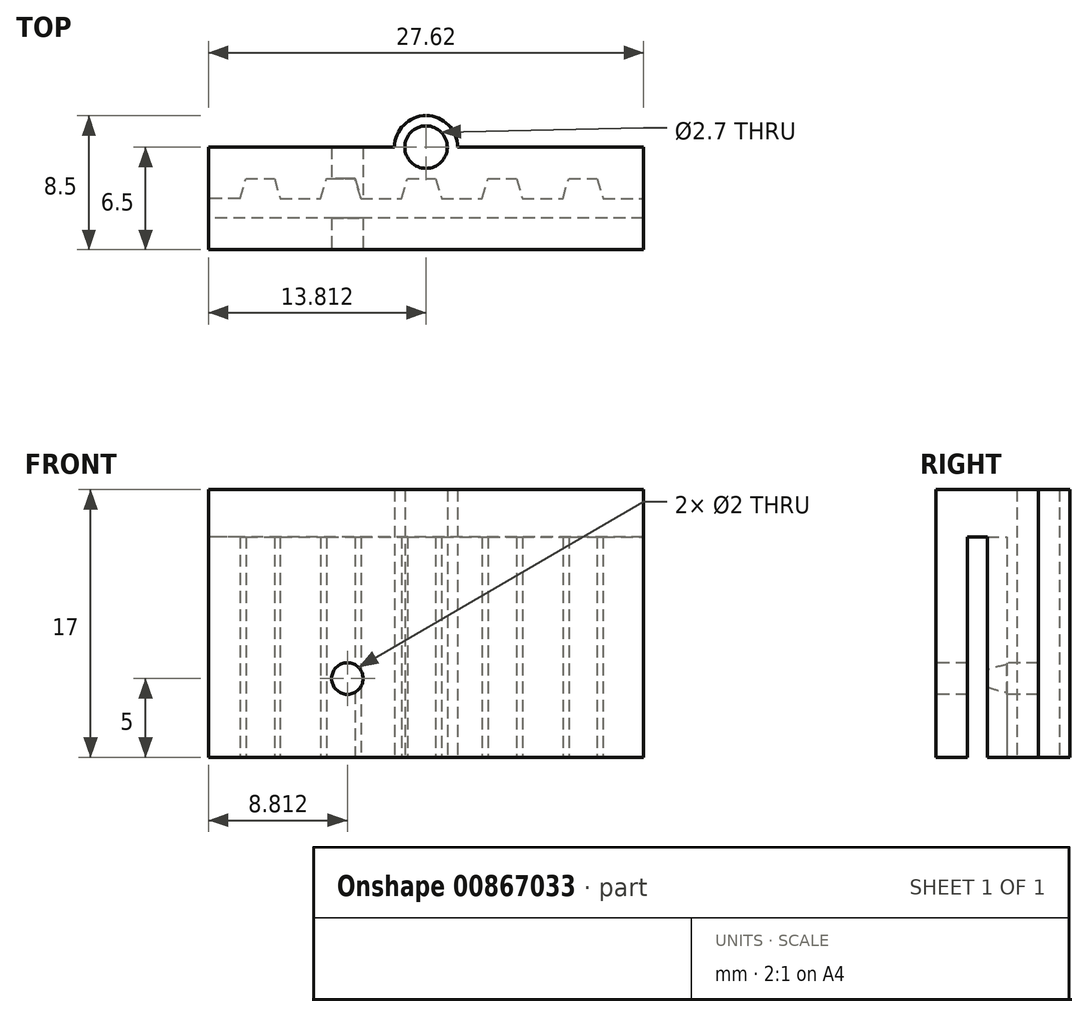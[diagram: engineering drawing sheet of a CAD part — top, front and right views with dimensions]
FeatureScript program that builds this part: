
annotation { "Feature Type Name" : "Feature", "Feature Type Description" : "" }
export const myFeature = defineFeature(function(context is Context, id is Id, definition is map)
    precondition{}
    {
        {
            var Q0;
            Q0=qCreatedBy(makeId("Top.planeOp"),FACE);
            var sketch = newSketch(context, id + "F0", { "sketchPlane" : qUnion([Q0])});
            skLineSegment(sketch, "E0", {"start": v(-20.5, 0) * mm, "end": v(-20.12, 1.25) * mm});
            skLineSegment(sketch, "E1", {"start": v(-20.12, 1.25) * mm, "end": v(-18.32, 1.25) * mm});
            skLineSegment(sketch, "E2", {"start": v(-18.33, 1.25) * mm, "end": v(-17.95, 0) * mm});
            skLineSegment(sketch, "E3", {"start": v(-19.22, 1.25) * mm, "end": v(-19.22, 0) * mm, "construction": true});
            skLineSegment(sketch, "E4", {"start": v(-20.5, -1.25) * mm, "end": v(5.13, -1.25) * mm});
            skLineSegment(sketch, "E5", {"start": v(-17.95, 0) * mm, "end": v(-15.37, 0) * mm});
            skLineSegment(sketch, "E6.1.0.0", {"start": v(-14.1, 1.25) * mm, "end": v(-14.1, 0) * mm, "construction": true});
            skLineSegment(sketch, "E6.1.0.1", {"start": v(-15, 1.25) * mm, "end": v(-13.2, 1.25) * mm});
            skLineSegment(sketch, "E6.1.0.2", {"start": v(-15.37, 0) * mm, "end": v(-15, 1.25) * mm});
            skLineSegment(sketch, "E6.1.0.3", {"start": v(-13.2, 1.25) * mm, "end": v(-12.82, 0) * mm});
            skLineSegment(sketch, "E6.1.0.4", {"start": v(-12.82, 0) * mm, "end": v(-10.25, 0) * mm});
            skLineSegment(sketch, "E6.2.0.0", {"start": v(-8.97, 1.25) * mm, "end": v(-8.97, 0) * mm, "construction": true});
            skLineSegment(sketch, "E6.2.0.1", {"start": v(-9.87, 1.25) * mm, "end": v(-8.07, 1.25) * mm});
            skLineSegment(sketch, "E6.2.0.2", {"start": v(-10.25, 0) * mm, "end": v(-9.87, 1.25) * mm});
            skLineSegment(sketch, "E6.2.0.3", {"start": v(-8.08, 1.25) * mm, "end": v(-7.7, 0) * mm});
            skLineSegment(sketch, "E6.2.0.4", {"start": v(-7.7, 0) * mm, "end": v(-5.12, 0) * mm});
            skLineSegment(sketch, "E6.3.0.0", {"start": v(-3.85, 1.25) * mm, "end": v(-3.85, 0) * mm, "construction": true});
            skLineSegment(sketch, "E6.3.0.1", {"start": v(-4.75, 1.25) * mm, "end": v(-2.95, 1.25) * mm});
            skLineSegment(sketch, "E6.3.0.2", {"start": v(-5.12, 0) * mm, "end": v(-4.75, 1.25) * mm});
            skLineSegment(sketch, "E6.3.0.3", {"start": v(-2.95, 1.25) * mm, "end": v(-2.57, 0) * mm});
            skLineSegment(sketch, "E6.3.0.4", {"start": v(-2.57, 0) * mm, "end": v(0, 0) * mm});
            skLineSegment(sketch, "E6.direction1", {"start": v(-20.5, 0) * mm, "end": v(-15.37, 0) * mm, "construction": true});
            skLineSegment(sketch, "E7.0.4.0", {"start": v(1.28, 1.25) * mm, "end": v(1.28, 0) * mm, "construction": true});
            skLineSegment(sketch, "E7.3.4.0", {"start": v(0.38, 1.25) * mm, "end": v(2.17, 1.25) * mm});
            skLineSegment(sketch, "E7.6.4.0", {"start": v(0, 0) * mm, "end": v(0.38, 1.25) * mm});
            skLineSegment(sketch, "E7.9.4.0", {"start": v(2.17, 1.25) * mm, "end": v(2.55, 0) * mm});
            skLineSegment(sketch, "E7.12.4.0", {"start": v(2.55, 0) * mm, "end": v(5.12, 0) * mm});
            skLineSegment(sketch, "E8", {"start": v(5.12, 0) * mm, "end": v(5.12, -1.25) * mm});
            skLineSegment(sketch, "E9", {"start": v(-20.5, 0) * mm, "end": v(-22.5, 0) * mm});
            skLineSegment(sketch, "E10", {"start": v(-22.5, 0) * mm, "end": v(-22.5, -1.25) * mm});
            skLineSegment(sketch, "E11", {"start": v(-20.5, -1.25) * mm, "end": v(-22.5, -1.25) * mm});
            skSolve(sketch);
        }
        {
            var Q0;
            Q0 = qSketchRegion(id + "F0", true);
            extrude(context, id + "F1", {"entities" : qUnion([Q0]), "depth" : 14 * mm, "offsetDistance" : 25 * mm});
        }
        {
            var Q0;
            Q0=qCreatedBy(makeId("Top.planeOp"),FACE);
            var sketch = newSketch(context, id + "F2", { "sketchPlane" : qUnion([Q0])});
            skLineSegment(sketch, "E12.bottom", {"start": v(5.13, 3.25) * mm, "end": v(-6.69, 3.25) * mm});
            skLineSegment(sketch, "E12.top", {"start": v(5.12, -3.25) * mm, "end": v(-22.5, -3.25) * mm});
            skLineSegment(sketch, "E12.left", {"start": v(5.12, 3.25) * mm, "end": v(5.12, -3.25) * mm});
            skLineSegment(sketch, "E12.right", {"start": v(-22.5, 3.25) * mm, "end": v(-22.5, -3.25) * mm});
            skArc(sketch, "E13", {"start": v(-6.69, 3.25) * mm, "mid": v(-8.69, 5.25) * mm, "end": v(-10.69, 3.25) * mm});
            skPoint(sketch, "E13.centerSnap0", {"position": v(-8.69, 3.25) * mm});
            skCircle(sketch, "E14", {"center": v(-8.69, 3.25) * mm, "radius": 1.35 * mm});
            skLineSegment(sketch, "E15.trimOffspring", {"start": v(-10.69, 3.25) * mm, "end": v(-22.5, 3.25) * mm});
            skSolve(sketch);
        }
        {
            var Q0;
            Q0 = qSketchRegion(id + "F2", true);
            extrude(context, id + "F3", {"entities" : qUnion([Q0]), "depth" : 17 * mm, "offsetDistance" : 25 * mm});
        }
        {
            var Q0;
            Q0=makeQuery(id+"F1.opExtrude","SWEPT_BODY",BODY,{"disambiguationData":[OSD([sQuery(id+"F0.wireOp",EDGE,"E0"),sQuery(id+"F0.wireOp",EDGE,"E1"),sQuery(id+"F0.wireOp",EDGE,"E2"),sQuery(id+"F0.wireOp",EDGE,"E4"),sQuery(id+"F0.wireOp",EDGE,"E5"),sQuery(id+"F0.wireOp",EDGE,"E6.1.0.1"),sQuery(id+"F0.wireOp",EDGE,"E6.1.0.2"),sQuery(id+"F0.wireOp",EDGE,"E6.1.0.3"),sQuery(id+"F0.wireOp",EDGE,"E6.1.0.4"),sQuery(id+"F0.wireOp",EDGE,"E6.2.0.1"),sQuery(id+"F0.wireOp",EDGE,"E6.2.0.2"),sQuery(id+"F0.wireOp",EDGE,"E6.2.0.3"),sQuery(id+"F0.wireOp",EDGE,"E6.2.0.4"),sQuery(id+"F0.wireOp",EDGE,"E6.3.0.1"),sQuery(id+"F0.wireOp",EDGE,"E6.3.0.2"),sQuery(id+"F0.wireOp",EDGE,"E6.3.0.3"),sQuery(id+"F0.wireOp",EDGE,"E6.3.0.4"),sQuery(id+"F0.wireOp",EDGE,"q5GiHhRO-Zi5s-ISNl-TxEt-K3SWIZUbKvAY"),sQuery(id+"F0.wireOp",EDGE,"yf0gqaRD-bWrP-ZFbW-EWTV-EAkCKsaRVM2o")])]});
            var Q1;
            Q1=makeQuery(id+"F3.opExtrude","SWEPT_BODY",BODY,{"disambiguationData":[OSD([sQuery(id+"F2.wireOp",EDGE,"E12.bottom"),sQuery(id+"F2.wireOp",EDGE,"E12.top"),sQuery(id+"F2.wireOp",EDGE,"E12.left"),sQuery(id+"F2.wireOp",EDGE,"E12.right")])]});
            booleanBodies(context, id + "F4", {"operationType" : BooleanOperationType.SUBTRACTION, "tools" : qUnion([Q0]), "targets" : qUnion([Q1])});
        }
        {
            var Q0;
            Q0=makeQuery(id+"F3.opExtrude","SWEPT_FACE",FACE,{"disambiguationData":[OSD([sQuery(id+"F2.wireOp",EDGE,"E12.top")])]});
            var sketch = newSketch(context, id + "F5", { "sketchPlane" : qUnion([Q0])});
            skCircle(sketch, "E16", {"center": v(-13.69, 5) * mm, "radius": 1 * mm});
            skPoint(sketch, "E16.centerSnap0", {"position": v(-8.69, 0) * mm});
            skSolve(sketch);
        }
        {
            var Q0;
            Q0 = qSketchRegion(id + "F5", true);
            extrude(context, id + "F6", {"entities" : qUnion([Q0]), "operationType" : NewBodyOperationType.REMOVE, "oppositeDirection" : true, "depth" : 25 * mm, "offsetDistance" : 25 * mm});
        }
    });
